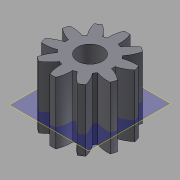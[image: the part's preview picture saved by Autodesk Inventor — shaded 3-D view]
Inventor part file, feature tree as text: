
AUTODESK INVENTOR PART (.ipt)
format: ipt  version: 2015 (Build 190159000, 159)  size: 180,736 bytes
history: native  units: mm (DEFAULTED — no unit token found)
features: plane x4, other x3, sketch x3, extrude x2
ambient origin geometry x8: Origin, YZ Plane, XZ Plane, XY Plane, X Axis, Y Axis, Z Axis, Center Point
bodies: Solid1 (feature_tree)
feature tree (12):
  extrude  "Extrusion1"  Depth=5.0mm TaperAngle=0.0deg
  plane  "Work Plane2"
  plane  "Work Plane8"
  plane  "Work Plane9"
  other  "Spur Gear"
  extrude  "Extrusion2"  Depth=10.0mm TaperAngle=0.0deg
  plane  "Work Plane12"
  sketch  "Sketch1"  dims[d0=6.0mm d1=5.0mm d2=0.0mm]
  sketch  "Sketch2"  dims[d3=5.0mm d4=10.0mm d5=0.0mm]
  other  "Srf1"
  sketch  "Sketch3"  dims[d16=12.0mm d17=0.0mm d34=3.141593mm d39=0.0mm d41=0.0mm d43=12.0mm d46=12.0mm d47=0.0mm d48=0.0mm d49=2.0mm d50=10.0mm d51=0.0mm d53=-1.5mm]
  other  "Pitch Diameter"
